# Revit family: Outlet-Bath-Dorf Enigma-Wall5487444c-394c-4278-a50f-5a49c127612d
name_source: partatom
category: Plumbing Fixtures
revit_build: Autodesk Revit 2015 (Build: 20140606_1530(x64)
units: mm (PartAtom-declared; Revit-internal decimal feet)

## types (2) — shared parameters
Assembly Code = C1030210
CW Connection = Yes
CWFU = 4
Connector Radius = 10 mm  [stored 0.0328084 ft]
Default Elevation = 500 mm  [stored 1.64042 ft]
HW Connection = Yes
HWFU = 4
Height_ANZRS = 55 mm  [stored 0.180446 ft]
Length_ANZRS = 55 mm  [stored 0.180446 ft]
Manufacturer = GWA Bathrooms & Kitchens
ModifiedIssue_ANZRS = 20160616 $
URL = http://specify.caroma.com.au
Vent Connection = No
Waste Connection = No
Width_ANZRS = 223 mm  [stored 0.731627 ft]
zero-valued in all types: Cost

## per-type parameters (varying)
| type | Material_ANZRS | Model | Type Comments |
| Chrome | Metal-Chrome-Caroma | 6592.04 | Dorf Enigma Bath Outlet |
| Black | Metal-Steel-Powdercoated-Matte Black | 6592.09 | Dorf Enigma Bath Outlet Black |

note: [stored X ft] marks values corroborated as IEEE doubles in the binary element streams (Revit-internal decimal feet)

## geometry (parser evidence)
native form markers: Blend x10, Sweep x2
no freeform markers — native parametric forms only
